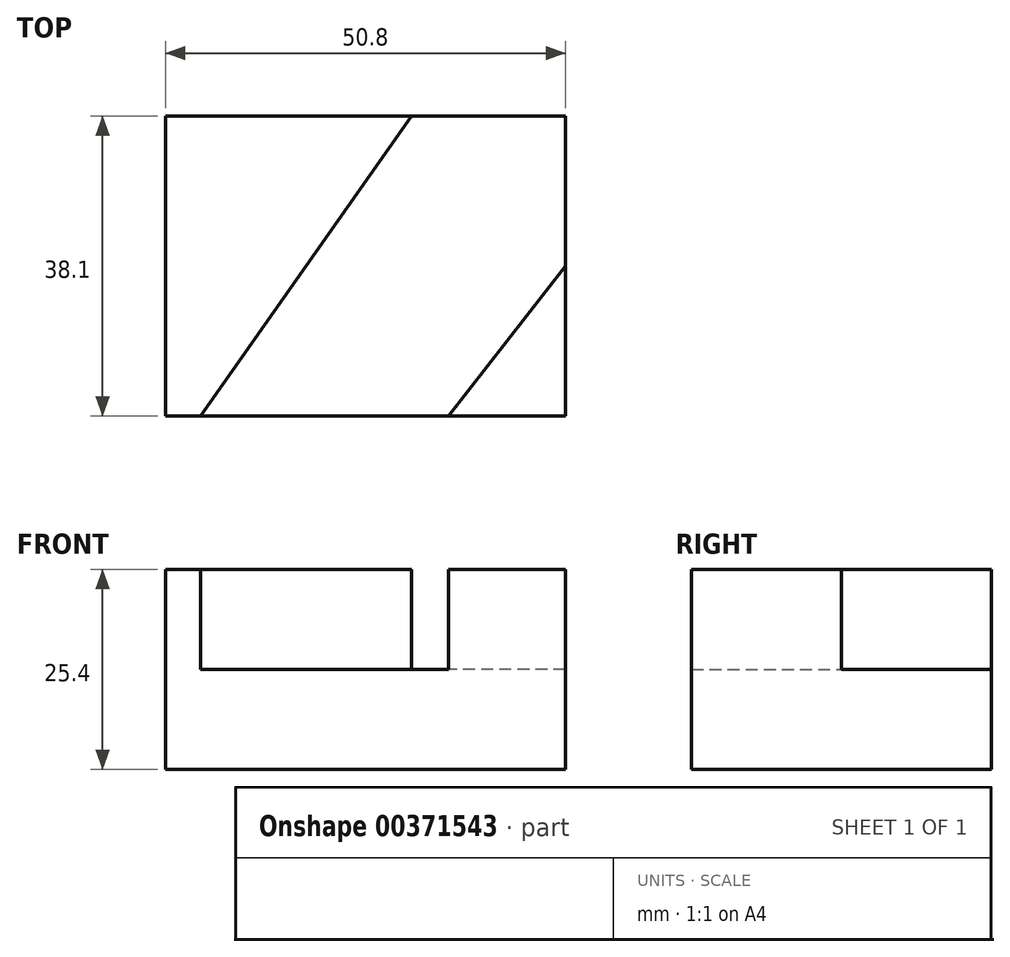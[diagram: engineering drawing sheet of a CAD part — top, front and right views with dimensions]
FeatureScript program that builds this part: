
annotation { "Feature Type Name" : "Feature", "Feature Type Description" : "" }
export const myFeature = defineFeature(function(context is Context, id is Id, definition is map)
    precondition{}
    {
        {
            var Q0;
            Q0=qCreatedBy(makeId("Front.planeOp"),FACE);
            var sketch = newSketch(context, id + "F0", { "sketchPlane" : qUnion([Q0])});
            skLineSegment(sketch, "E0", {"start": v(0, 0) * mm, "end": v(50.8, 0) * mm});
            skLineSegment(sketch, "E1", {"start": v(50.8, 0) * mm, "end": v(50.8, 25.4) * mm});
            skLineSegment(sketch, "E2", {"start": v(50.8, 25.4) * mm, "end": v(0, 25.4) * mm});
            skLineSegment(sketch, "E3", {"start": v(0, 25.4) * mm, "end": v(0, 0) * mm});
            skSolve(sketch);
        }
        {
            var Q0;
            Q0=makeQuery(id+"F0.imprint","IMPRINT",FACE,{"disambiguationData":[TD([[makeQuery(id+"F0.imprint","IMPRINT",EDGE,{"derivedFrom":sQuery(id+"F0.wireOp",EDGE,"E0")}),1.0]])]});
            extrude(context, id + "F1", {"entities" : qUnion([Q0]), "depth" : 38.1 * mm});
        }
        {
            var Q0;
            Q0=makeQuery(id+"F1.opExtrude","SWEPT_FACE",FACE,{"disambiguationData":[OSD([sQuery(id+"F0.wireOp",EDGE,"E2")])]});
            var sketch = newSketch(context, id + "F2", { "sketchPlane" : qUnion([Q0])});
            skLineSegment(sketch, "E4", {"start": v(0, -38.1) * mm, "end": v(4.42, -38.1) * mm});
            skLineSegment(sketch, "E5", {"start": v(4.42, -38.1) * mm, "end": v(31.26, 0) * mm});
            skLineSegment(sketch, "E6", {"start": v(31.26, 0) * mm, "end": v(0, 0) * mm});
            skLineSegment(sketch, "E7", {"start": v(0, 0) * mm, "end": v(0, -38.1) * mm});
            skLineSegment(sketch, "E8", {"start": v(4.42, -38.1) * mm, "end": v(35.96, -38.1) * mm});
            skLineSegment(sketch, "E9", {"start": v(31.26, 0) * mm, "end": v(50.8, 0) * mm});
            skLineSegment(sketch, "E10", {"start": v(50.8, 0) * mm, "end": v(50.8, -19.05) * mm});
            skLineSegment(sketch, "E11", {"start": v(50.8, -19.05) * mm, "end": v(35.96, -38.1) * mm});
            skSolve(sketch);
        }
        {
            var Q0;
            Q0=makeQuery(id+"F2.imprint","IMPRINT",FACE,{"disambiguationData":[TD([[makeQuery(id+"F2.imprint","IMPRINT",EDGE,{"derivedFrom":sQuery(id+"F2.wireOp",EDGE,"E5")}),-1.0]])]});
            extrude(context, id + "F3", {"entities" : qUnion([Q0]), "operationType" : NewBodyOperationType.REMOVE, "oppositeDirection" : true, "depth" : 12.7 * mm});
        }
    });
